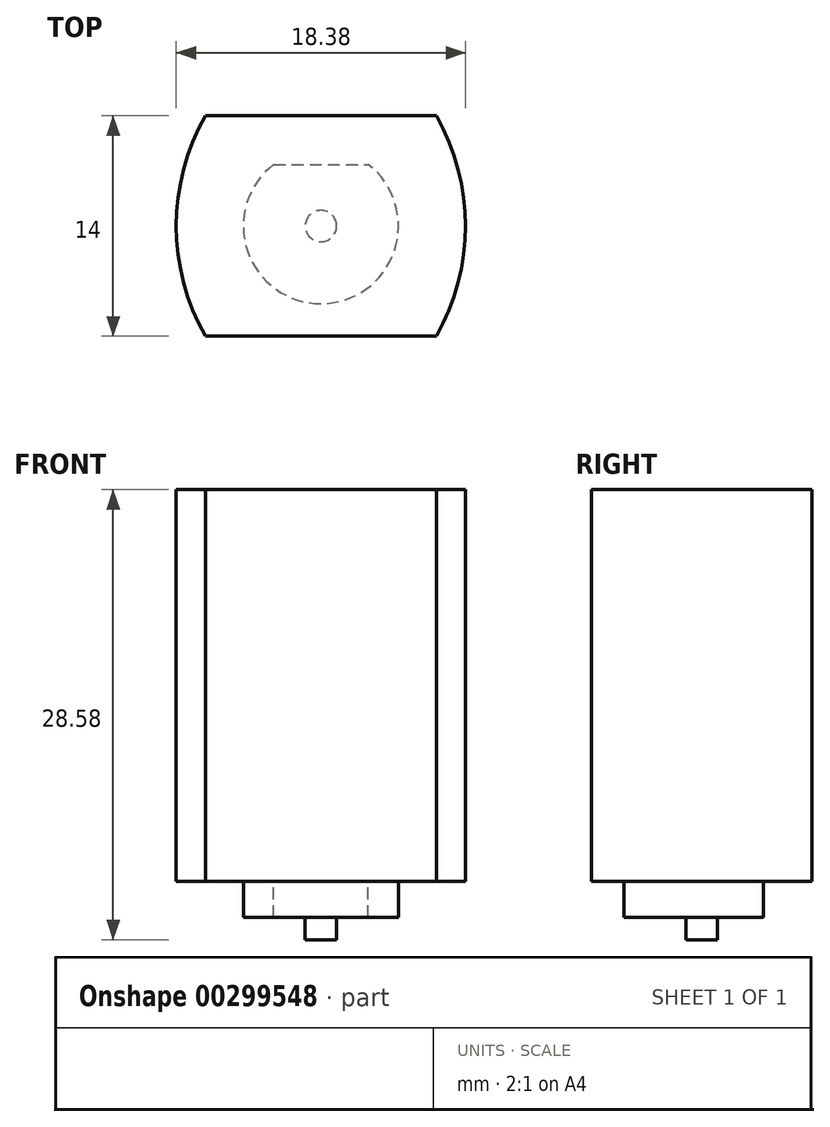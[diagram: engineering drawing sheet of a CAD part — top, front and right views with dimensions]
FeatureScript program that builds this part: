
annotation { "Feature Type Name" : "Feature", "Feature Type Description" : "" }
export const myFeature = defineFeature(function(context is Context, id is Id, definition is map)
    precondition{}
    {
        {
            var Q0;
            Q0=qCreatedBy(makeId("Top.planeOp"),FACE);
            var sketch = newSketch(context, id + "F0", { "sketchPlane" : qUnion([Q0])});
            skLineSegment(sketch, "E0.bottom", {"start": v(9.19, -7) * mm, "end": v(-9.19, -7) * mm});
            skLineSegment(sketch, "E0.top", {"start": v(9.19, 7) * mm, "end": v(-9.19, 7) * mm});
            skLineSegment(sketch, "E0.left", {"start": v(9.19, -7) * mm, "end": v(9.19, 7) * mm});
            skLineSegment(sketch, "E0.right", {"start": v(-9.19, -7) * mm, "end": v(-9.19, 7) * mm});
            skPoint(sketch, "E0.middle", {"position": v(0, 0) * mm});
            skLineSegment(sketch, "E1", {"start": v(-7.33, 7) * mm, "end": v(-7.33, -7) * mm, "construction": true});
            skLineSegment(sketch, "E2.MirrorCS", {"start": v(7.33, 7) * mm, "end": v(7.33, -7) * mm, "construction": true});
            skPoint(sketch, "E3", {"position": v(-9.19, 0) * mm});
            skArc(sketch, "E4", {"start": v(-7.33, 7) * mm, "mid": v(-9.19, 0) * mm, "end": v(-7.33, -7) * mm});
            skArc(sketch, "E5.MirrorCS", {"start": v(7.33, 7) * mm, "mid": v(9.19, 0) * mm, "end": v(7.33, -7) * mm});
            skSolve(sketch);
        }
        {
            var Q0;
            {var subQ0=sQuery(id+"F0.wireOp",EDGE,"E4");var subQ1=sQuery(id+"F0.wireOp",EDGE,"E0.bottom");var subQ2=makeQuery(id+"F0.imprint","INTERSECT",VERTEX,{"derivedFrom":[subQ1,subQ0]});Q0=makeQuery(id+"F0.imprint","IMPRINT",FACE,{"disambiguationData":[TD([[makeQuery(id+"F0.imprint","IMPRINT",EDGE,{"disambiguationData":[TD([[subQ2,1.0]])],"derivedFrom":subQ1}),-1.0]])]});}
            extrude(context, id + "F1", {"entities" : qUnion([Q0]), "endBound" : BoundingType.SYMMETRIC, "depth" : 24.88 * mm});
        }
        {
            var Q0;
            Q0=makeQuery(id+"F1.opExtrude","CAP_FACE",FACE,{"disambiguationData":[OSD([sQuery(id+"F0.wireOp",EDGE,"E0.bottom"),sQuery(id+"F0.wireOp",EDGE,"E0.top"),sQuery(id+"F0.wireOp",EDGE,"E4"),sQuery(id+"F0.wireOp",EDGE,"E5.MirrorCS")])],"isStart":true});
            var sketch = newSketch(context, id + "F2", { "sketchPlane" : qUnion([Q0])});
            skCircle(sketch, "E6", {"center": v(0, 0) * mm, "radius": 4.93 * mm});
            skLineSegment(sketch, "E7", {"start": v(0, 4.93) * mm, "end": v(0, -3.91) * mm, "construction": true});
            skLineSegment(sketch, "E8", {"start": v(-3, -3.91) * mm, "end": v(3, -3.91) * mm});
            skSolve(sketch);
        }
        {
            var Q0;
            {var subQ0=sQuery(id+"F2.wireOp",EDGE,"E8");Q0=makeQuery(id+"F2.imprint","IMPRINT",FACE,{"disambiguationData":[TD([[makeQuery(id+"F2.imprint","IMPRINT",EDGE,{"derivedFrom":subQ0}),1.0]])]});}
            extrude(context, id + "F3", {"entities" : qUnion([Q0]), "operationType" : NewBodyOperationType.ADD, "depth" : 2.28 * mm});
        }
        {
            var Q0;
            Q0=makeQuery(id+"F3.opExtrude","CAP_FACE",FACE,{"disambiguationData":[OSD([sQuery(id+"F2.wireOp",EDGE,"E6"),sQuery(id+"F2.wireOp",EDGE,"E8")])],"isStart":false});
            var sketch = newSketch(context, id + "F4", { "sketchPlane" : qUnion([Q0])});
            skCircle(sketch, "E9", {"center": v(0, 0) * mm, "radius": 1 * mm});
            skSolve(sketch);
        }
        {
            var Q0;
            Q0=makeQuery(id+"F4.imprint","IMPRINT",FACE,{"disambiguationData":[TD([[makeQuery(id+"F4.imprint","IMPRINT",EDGE,{"derivedFrom":sQuery(id+"F4.wireOp",EDGE,"E9")}),1.0]])]});
            extrude(context, id + "F5", {"entities" : qUnion([Q0]), "operationType" : NewBodyOperationType.ADD, "depth" : 1.42 * mm});
        }
    });
